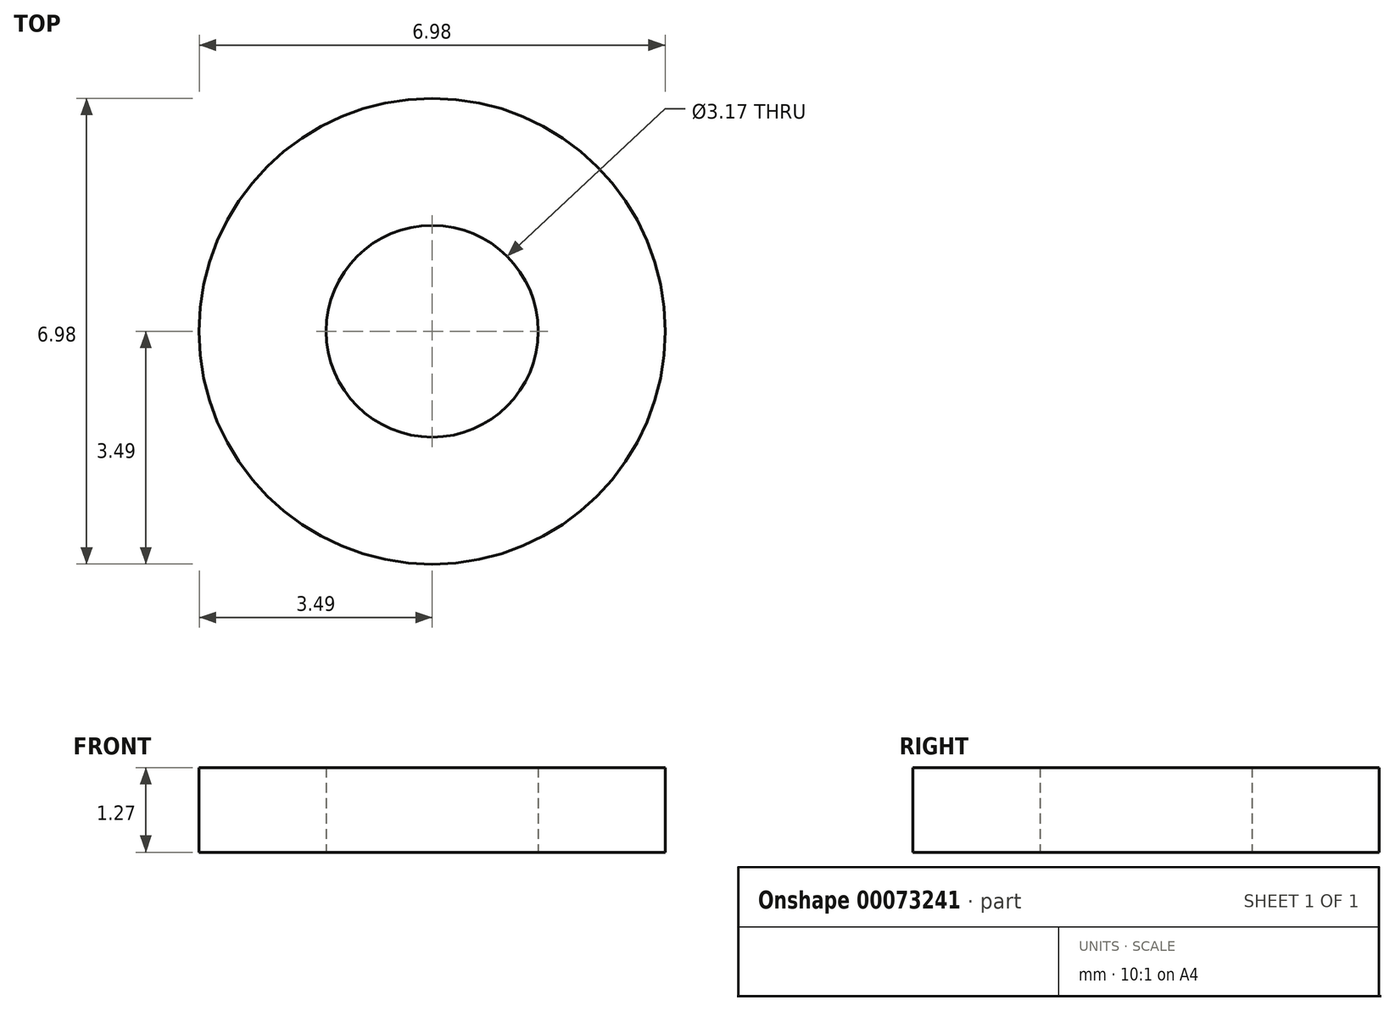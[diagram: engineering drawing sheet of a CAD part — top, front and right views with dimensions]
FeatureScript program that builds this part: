
annotation { "Feature Type Name" : "Feature", "Feature Type Description" : "" }
export const myFeature = defineFeature(function(context is Context, id is Id, definition is map)
    precondition{}
    {
        {
            var Q0;
            Q0=qCreatedBy(makeId("Top.planeOp"),FACE);
            var sketch = newSketch(context, id + "F0", { "sketchPlane" : qUnion([Q0])});
            skCircle(sketch, "E0", {"center": v(0, 0) * mm, "radius": 1.59 * mm});
            skCircle(sketch, "E1", {"center": v(0, 0) * mm, "radius": 3.5 * mm});
            skSolve(sketch);
        }
        {
            var Q0;
            Q0 = qSketchRegion(id + "F0", true);
            extrude(context, id + "F1", {"entities" : qUnion([Q0]), "depth" : 1.27 * mm});
        }
    });
